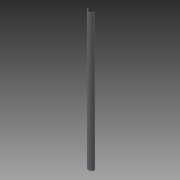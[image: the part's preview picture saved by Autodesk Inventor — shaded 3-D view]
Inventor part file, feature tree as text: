
AUTODESK INVENTOR PART (.ipt)
format: ipt  version: 2015 SP1 (Build 190203100, 203)  size: 87,552 bytes
history: native  units: mm
features: extrude x2, sketch x2
ambient origin geometry x8: Origin, YZ Plane, XZ Plane, XY Plane, X Axis, Y Axis, Z Axis, Center Point
bodies: Solid1 (feature_tree)
feature tree (4):
  extrude  "Extrusion1"  Depth=100.0mm
  extrude  "Extrusion2"  Depth=10.0mm
  sketch  "Sketch1"  dims[d0=3.0mm d1=100.0mm]
  sketch  "Sketch2"  dims[d2=2000.0mm d3=0.0mm d4=4.0mm d5=20.0mm d6=10.0mm d7=0.0mm d8=0.0mm]
